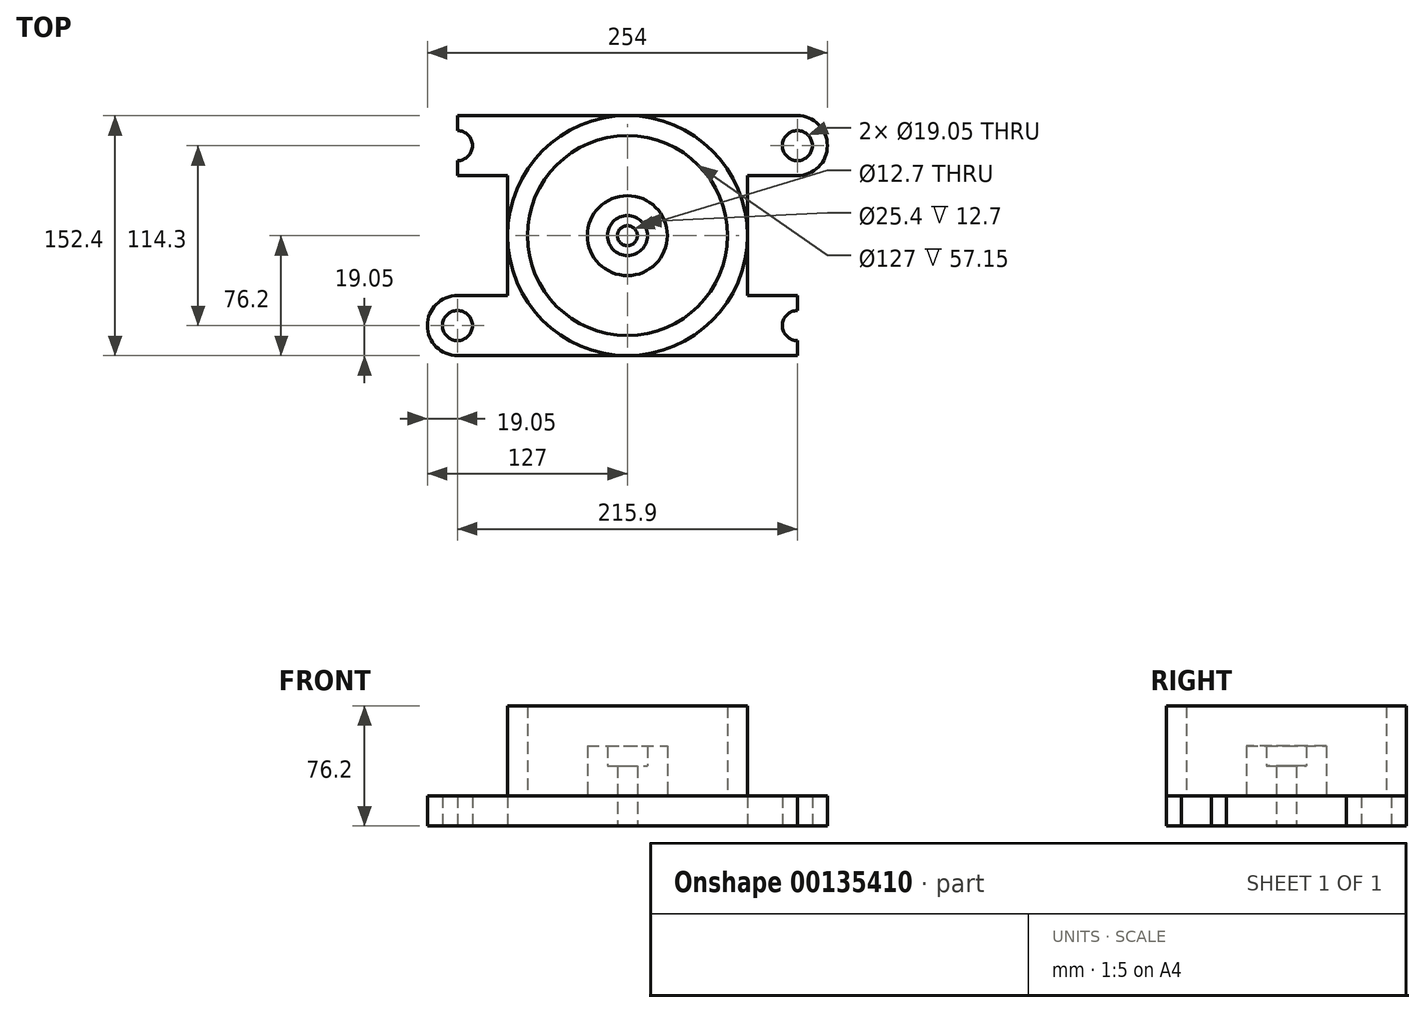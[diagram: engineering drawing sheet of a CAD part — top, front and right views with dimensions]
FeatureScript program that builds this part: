
annotation { "Feature Type Name" : "Feature", "Feature Type Description" : "" }
export const myFeature = defineFeature(function(context is Context, id is Id, definition is map)
    precondition{}
    {
        {
            var Q0;
            Q0=qCreatedBy(makeId("Front.planeOp"),FACE);
            var sketch = newSketch(context, id + "F0", { "sketchPlane" : qUnion([Q0])});
            skLineSegment(sketch, "E0", {"start": v(-6.35, 0) * mm, "end": v(-76.2, 0) * mm});
            skLineSegment(sketch, "E1", {"start": v(-76.2, 0) * mm, "end": v(-76.2, 76.2) * mm});
            skLineSegment(sketch, "E2", {"start": v(-76.2, 76.2) * mm, "end": v(-63.5, 76.2) * mm});
            skLineSegment(sketch, "E3", {"start": v(-63.5, 76.2) * mm, "end": v(-63.5, 19.05) * mm});
            skLineSegment(sketch, "E4", {"start": v(-63.5, 19.05) * mm, "end": v(-25.4, 19.05) * mm});
            skLineSegment(sketch, "E5", {"start": v(-25.4, 19.05) * mm, "end": v(-25.4, 50.8) * mm});
            skLineSegment(sketch, "E6", {"start": v(-25.4, 50.8) * mm, "end": v(-12.7, 50.8) * mm});
            skLineSegment(sketch, "E7", {"start": v(-12.7, 50.8) * mm, "end": v(-12.7, 38.1) * mm});
            skLineSegment(sketch, "E8", {"start": v(-12.7, 38.1) * mm, "end": v(-6.35, 38.1) * mm});
            skLineSegment(sketch, "E9", {"start": v(-6.35, 38.1) * mm, "end": v(-6.35, 0) * mm});
            skLineSegment(sketch, "E10", {"start": v(0, 0) * mm, "end": v(0, 68) * mm});
            skSolve(sketch);
        }
        {
            var Q0;
            Q0=makeQuery(id+"F0.imprint","IMPRINT",FACE,{"disambiguationData":[TD([[makeQuery(id+"F0.imprint","IMPRINT",EDGE,{"derivedFrom":sQuery(id+"F0.wireOp",EDGE,"E0")}),-1.0]])]});
            var Q1;
            Q1=sQuery(id+"F0.wireOp",EDGE,"E10");
            revolve(context, id + "F1", {"entities" : qUnion([Q0]), "axis" : qUnion([Q1]), "revolveType" : RevolveType.FULL});
        }
        {
            var Q0;
            Q0=qCreatedBy(makeId("Top.planeOp"),FACE);
            var sketch = newSketch(context, id + "F2", { "sketchPlane" : qUnion([Q0])});
            skCircle(sketch, "E11.0", {"center": v(0, 0) * mm, "radius": 76.2 * mm});
            skLineSegment(sketch, "E12", {"start": v(0, -76.2) * mm, "end": v(-107.95, -76.2) * mm});
            skLineSegment(sketch, "E13", {"start": v(-107.95, -76.2) * mm, "end": v(-107.95, -66.68) * mm});
            skLineSegment(sketch, "E14", {"start": v(-107.95, -38.1) * mm, "end": v(-76.2, -38.1) * mm});
            skLineSegment(sketch, "E15", {"start": v(-76.2, -38.1) * mm, "end": v(-76.2, 0) * mm});
            skArc(sketch, "E16", {"start": v(-107.95, -38.1) * mm, "mid": v(-127, -57.15) * mm, "end": v(-107.95, -76.2) * mm});
            skCircle(sketch, "E17", {"center": v(-107.95, -57.15) * mm, "radius": 9.53 * mm});
            skLineSegment(sketch, "E18.trimOffspring", {"start": v(-107.95, -47.63) * mm, "end": v(-107.95, -38.1) * mm});
            skLineSegment(sketch, "E19.MirrorCS", {"start": v(-107.95, 38.1) * mm, "end": v(-76.2, 38.1) * mm});
            skLineSegment(sketch, "E20.MirrorCS", {"start": v(-76.2, 38.1) * mm, "end": v(-76.2, 0) * mm});
            skLineSegment(sketch, "E21.MirrorCS", {"start": v(0, 76.2) * mm, "end": v(-107.95, 76.2) * mm});
            skArc(sketch, "E22.MirrorCS", {"start": v(-107.95, 38.1) * mm, "mid": v(-127, 57.15) * mm, "end": v(-107.95, 76.2) * mm});
            skCircle(sketch, "E23.MirrorC", {"center": v(-107.95, 57.15) * mm, "radius": 9.53 * mm});
            skLineSegment(sketch, "E24.MirrorCS", {"start": v(-107.95, 47.63) * mm, "end": v(-107.95, 38.1) * mm});
            skLineSegment(sketch, "E25.MirrorCS", {"start": v(-107.95, 76.2) * mm, "end": v(-107.95, 66.68) * mm});
            skLineSegment(sketch, "E26.MirrorCS", {"start": v(107.95, 38.1) * mm, "end": v(76.2, 38.1) * mm});
            skLineSegment(sketch, "E27.MirrorCS", {"start": v(107.95, 47.63) * mm, "end": v(107.95, 38.1) * mm});
            skArc(sketch, "E28.MirrorCS", {"start": v(107.95, 38.1) * mm, "mid": v(127, 57.15) * mm, "end": v(107.95, 76.2) * mm});
            skCircle(sketch, "E29.MirrorC", {"center": v(107.95, 57.15) * mm, "radius": 9.53 * mm});
            skLineSegment(sketch, "E30.MirrorCS", {"start": v(107.95, 76.2) * mm, "end": v(107.95, 66.68) * mm});
            skLineSegment(sketch, "E31.MirrorCS", {"start": v(0, 76.2) * mm, "end": v(107.95, 76.2) * mm});
            skLineSegment(sketch, "E32.MirrorCS", {"start": v(76.2, 38.1) * mm, "end": v(76.2, 0) * mm});
            skLineSegment(sketch, "E33.MirrorCS", {"start": v(107.95, -38.1) * mm, "end": v(76.2, -38.1) * mm});
            skLineSegment(sketch, "E34.MirrorCS", {"start": v(76.2, -38.1) * mm, "end": v(76.2, 0) * mm});
            skArc(sketch, "E35.MirrorCS", {"start": v(107.95, -38.1) * mm, "mid": v(127, -57.15) * mm, "end": v(107.95, -76.2) * mm});
            skCircle(sketch, "E36.MirrorC", {"center": v(107.95, -57.15) * mm, "radius": 9.53 * mm});
            skLineSegment(sketch, "E37.MirrorCS", {"start": v(107.95, -47.63) * mm, "end": v(107.95, -38.1) * mm});
            skLineSegment(sketch, "E38.MirrorCS", {"start": v(107.95, -76.2) * mm, "end": v(107.95, -66.68) * mm});
            skLineSegment(sketch, "E39.MirrorCS", {"start": v(0, -76.2) * mm, "end": v(107.95, -76.2) * mm});
            skSolve(sketch);
        }
        {
            var Q0;
            Q0=makeQuery(id+"F2.imprint","IMPRINT",FACE,{"disambiguationData":[TD([[makeQuery(id+"F2.imprint","IMPRINT",EDGE,{"derivedFrom":sQuery(id+"F2.wireOp",EDGE,"E19.MirrorCS")}),1.0]])]});
            var Q1;
            Q1=makeQuery(id+"F2.imprint","IMPRINT",FACE,{"disambiguationData":[TD([[makeQuery(id+"F2.imprint","IMPRINT",EDGE,{"derivedFrom":sQuery(id+"F2.wireOp",EDGE,"E22.MirrorCS")}),-1.0]])]});
            var Q2;
            {var subQ2=sQuery(id+"F2.wireOp",EDGE,"E12");Q2=makeQuery(id+"F2.imprint","IMPRINT",FACE,{"disambiguationData":[TD([[makeQuery(id+"F2.imprint","IMPRINT",EDGE,{"derivedFrom":subQ2}),-1.0]])]});}
            var Q3;
            {var subQ0=sQuery(id+"F2.wireOp",EDGE,"E13");Q3=makeQuery(id+"F2.imprint","IMPRINT",FACE,{"disambiguationData":[TD([[makeQuery(id+"F2.imprint","IMPRINT",EDGE,{"derivedFrom":subQ0}),1.0]])]});}
            var Q4;
            Q4=makeQuery(id+"F2.imprint","IMPRINT",FACE,{"disambiguationData":[TD([[makeQuery(id+"F2.imprint","IMPRINT",EDGE,{"derivedFrom":sQuery(id+"F2.wireOp",EDGE,"E33.MirrorCS")}),1.0]])]});
            var Q5;
            Q5=makeQuery(id+"F2.imprint","IMPRINT",FACE,{"disambiguationData":[TD([[makeQuery(id+"F2.imprint","IMPRINT",EDGE,{"derivedFrom":sQuery(id+"F2.wireOp",EDGE,"E35.MirrorCS")}),-1.0]])]});
            var Q6;
            Q6=makeQuery(id+"F2.imprint","IMPRINT",FACE,{"disambiguationData":[TD([[makeQuery(id+"F2.imprint","IMPRINT",EDGE,{"derivedFrom":sQuery(id+"F2.wireOp",EDGE,"E26.MirrorCS")}),-1.0]])]});
            var Q7;
            {var subQ0=sQuery(id+"F2.wireOp",EDGE,"E27.MirrorCS");Q7=makeQuery(id+"F2.imprint","IMPRINT",FACE,{"disambiguationData":[TD([[makeQuery(id+"F2.imprint","IMPRINT",EDGE,{"derivedFrom":subQ0}),1.0]])]});}
            extrude(context, id + "F3", {"entities" : qUnion([Q0, Q1, Q2, Q3, Q4, Q5, Q6, Q7]), "operationType" : NewBodyOperationType.ADD, "depth" : 19.05 * mm});
        }
    });
